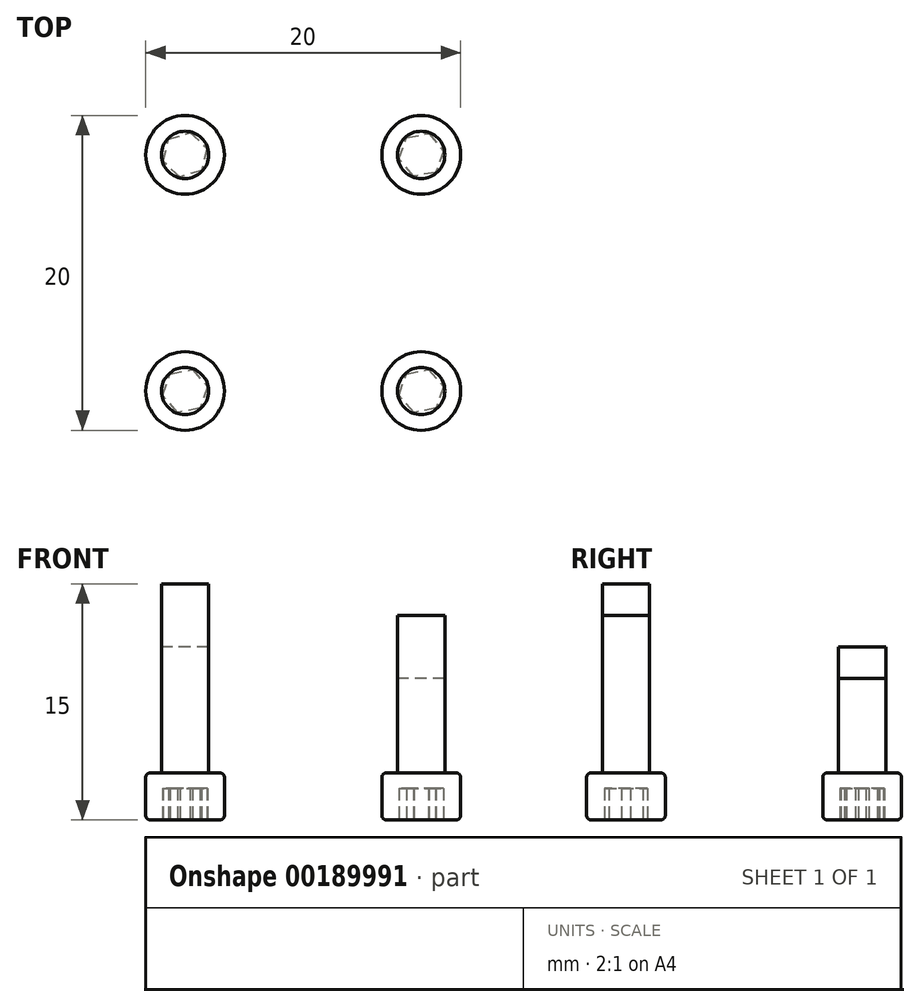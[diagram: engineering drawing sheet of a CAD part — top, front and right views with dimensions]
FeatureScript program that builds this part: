
annotation { "Feature Type Name" : "Feature", "Feature Type Description" : "" }
export const myFeature = defineFeature(function(context is Context, id is Id, definition is map)
    precondition{}
    {
        {
            var Q0;
            Q0=qCreatedBy(makeId("Top.planeOp"),FACE);
            var sketch = newSketch(context, id + "F0", { "sketchPlane" : qUnion([Q0])});
            skLineSegment(sketch, "E0.bottom", {"start": v(7.5, -7.5) * mm, "end": v(-7.5, -7.5) * mm, "construction": true});
            skLineSegment(sketch, "E0.top", {"start": v(7.5, 7.5) * mm, "end": v(-7.5, 7.5) * mm, "construction": true});
            skLineSegment(sketch, "E0.left", {"start": v(7.5, -7.5) * mm, "end": v(7.5, 7.5) * mm, "construction": true});
            skLineSegment(sketch, "E0.right", {"start": v(-7.5, -7.5) * mm, "end": v(-7.5, 7.5) * mm, "construction": true});
            skPoint(sketch, "E0.middle", {"position": v(0, 0) * mm});
            skCircle(sketch, "E1.cCircle", {"center": v(-7.5, 7.5) * mm, "radius": 1.44 * mm, "construction": true});
            skLineSegment(sketch, "E1.0", {"start": v(-6.45, 6.51) * mm, "end": v(-7.83, 6.1) * mm});
            skLineSegment(sketch, "E1.1", {"start": v(-7.83, 6.1) * mm, "end": v(-8.88, 7.08) * mm});
            skLineSegment(sketch, "E1.2", {"start": v(-8.88, 7.08) * mm, "end": v(-8.55, 8.49) * mm});
            skLineSegment(sketch, "E1.3", {"start": v(-8.55, 8.49) * mm, "end": v(-7.17, 8.9) * mm});
            skLineSegment(sketch, "E1.4", {"start": v(-7.17, 8.9) * mm, "end": v(-6.12, 7.92) * mm});
            skLineSegment(sketch, "E1.5", {"start": v(-6.12, 7.92) * mm, "end": v(-6.45, 6.51) * mm});
            skCircle(sketch, "E2.cCircle", {"center": v(7.5, 7.5) * mm, "radius": 1.44 * mm, "construction": true});
            skLineSegment(sketch, "E2.0", {"start": v(8.42, 6.39) * mm, "end": v(7, 6.15) * mm});
            skLineSegment(sketch, "E2.1", {"start": v(7, 6.15) * mm, "end": v(6.08, 7.26) * mm});
            skLineSegment(sketch, "E2.2", {"start": v(6.08, 7.26) * mm, "end": v(6.58, 8.61) * mm});
            skLineSegment(sketch, "E2.3", {"start": v(6.58, 8.61) * mm, "end": v(8, 8.85) * mm});
            skLineSegment(sketch, "E2.4", {"start": v(8, 8.85) * mm, "end": v(8.92, 7.74) * mm});
            skLineSegment(sketch, "E2.5", {"start": v(8.92, 7.74) * mm, "end": v(8.42, 6.39) * mm});
            skCircle(sketch, "E3.cCircle", {"center": v(-7.5, -7.5) * mm, "radius": 1.44 * mm, "construction": true});
            skLineSegment(sketch, "E3.0", {"start": v(-6.55, -8.6) * mm, "end": v(-7.97, -8.86) * mm});
            skLineSegment(sketch, "E3.1", {"start": v(-7.97, -8.86) * mm, "end": v(-8.92, -7.77) * mm});
            skLineSegment(sketch, "E3.2", {"start": v(-8.92, -7.77) * mm, "end": v(-8.45, -6.4) * mm});
            skLineSegment(sketch, "E3.3", {"start": v(-8.45, -6.4) * mm, "end": v(-7.03, -6.14) * mm});
            skLineSegment(sketch, "E3.4", {"start": v(-7.03, -6.14) * mm, "end": v(-6.08, -7.23) * mm});
            skLineSegment(sketch, "E3.5", {"start": v(-6.08, -7.23) * mm, "end": v(-6.55, -8.6) * mm});
            skCircle(sketch, "E4.cCircle", {"center": v(7.5, -7.5) * mm, "radius": 1.44 * mm, "construction": true});
            skLineSegment(sketch, "E4.0", {"start": v(8.45, -8.6) * mm, "end": v(7.03, -8.86) * mm});
            skLineSegment(sketch, "E4.1", {"start": v(7.03, -8.86) * mm, "end": v(6.08, -7.77) * mm});
            skLineSegment(sketch, "E4.2", {"start": v(6.08, -7.77) * mm, "end": v(6.55, -6.4) * mm});
            skLineSegment(sketch, "E4.3", {"start": v(6.55, -6.4) * mm, "end": v(7.97, -6.14) * mm});
            skLineSegment(sketch, "E4.4", {"start": v(7.97, -6.14) * mm, "end": v(8.92, -7.23) * mm});
            skLineSegment(sketch, "E4.5", {"start": v(8.92, -7.23) * mm, "end": v(8.45, -8.6) * mm});
            skCircle(sketch, "E5", {"center": v(-7.5, -7.5) * mm, "radius": 2.5 * mm});
            skCircle(sketch, "E6", {"center": v(7.5, -7.5) * mm, "radius": 2.5 * mm});
            skCircle(sketch, "E7", {"center": v(-7.5, 7.5) * mm, "radius": 2.5 * mm});
            skCircle(sketch, "E8", {"center": v(7.5, 7.5) * mm, "radius": 2.5 * mm});
            skSolve(sketch);
        }
        {
            var Q0;
            Q0 = qSketchRegion(id + "F0", true);
            extrude(context, id + "F1", {"entities" : qUnion([Q0]), "depth" : 2 * mm});
        }
        {
            var Q0;
            Q0=qCreatedBy(makeId("Top.planeOp"),FACE);
            cPlane(context, id + "F2", {"entities" : qUnion([Q0]), "cplaneType" : CPlaneType.OFFSET, "offset" : 2 * mm, "width" : 150 * mm, "height" : 150 * mm});
        }
        {
            var Q0;
            Q0=qCreatedBy(id+"F2.planeOp",FACE);
            var sketch = newSketch(context, id + "F3", { "sketchPlane" : qUnion([Q0])});
            skCircle(sketch, "E9.0", {"center": v(-7.5, 7.5) * mm, "radius": 2.5 * mm});
            skCircle(sketch, "E10.0", {"center": v(-7.5, -7.5) * mm, "radius": 2.5 * mm});
            skCircle(sketch, "E11.0", {"center": v(7.5, -7.5) * mm, "radius": 2.5 * mm});
            skCircle(sketch, "E12.0", {"center": v(7.5, 7.5) * mm, "radius": 2.5 * mm});
            skSolve(sketch);
        }
        {
            var Q0;
            Q0 = qSketchRegion(id + "F3", true);
            extrude(context, id + "F4", {"entities" : qUnion([Q0]), "operationType" : NewBodyOperationType.ADD, "depth" : 1 * mm});
        }
        {
            var Q0;
            Q0=qCreatedBy(id+"F2.planeOp",FACE);
            cPlane(context, id + "F5", {"entities" : qUnion([Q0]), "cplaneType" : CPlaneType.OFFSET, "offset" : 1 * mm, "width" : 150 * mm, "height" : 150 * mm});
        }
        {
            var Q0;
            Q0=qCreatedBy(id+"F5.planeOp",FACE);
            var sketch = newSketch(context, id + "F6", { "sketchPlane" : qUnion([Q0])});
            skPoint(sketch, "E13.0", {"position": v(7.5, 7.5) * mm});
            skCircle(sketch, "E14", {"center": v(7.5, 7.5) * mm, "radius": 1.5 * mm});
            skPoint(sketch, "E15.0", {"position": v(7.5, -7.5) * mm});
            skCircle(sketch, "E16", {"center": v(7.5, -7.5) * mm, "radius": 1.5 * mm});
            skPoint(sketch, "E17.0", {"position": v(-7.5, -7.5) * mm});
            skCircle(sketch, "E18", {"center": v(-7.5, -7.5) * mm, "radius": 1.5 * mm});
            skPoint(sketch, "E19.0", {"position": v(-7.5, 7.5) * mm});
            skCircle(sketch, "E20", {"center": v(-7.5, 7.5) * mm, "radius": 1.5 * mm});
            skSolve(sketch);
        }
        {
            var Q0;
            Q0=makeQuery(id+"F6.imprint","IMPRINT",FACE,{"disambiguationData":[TD([[makeQuery(id+"F6.imprint","IMPRINT",EDGE,{"derivedFrom":sQuery(id+"F6.wireOp",EDGE,"E14")}),1.0]])]});
            extrude(context, id + "F7", {"entities" : qUnion([Q0]), "operationType" : NewBodyOperationType.ADD, "depth" : 6 * mm});
        }
        {
            var Q0;
            Q0=makeQuery(id+"F6.imprint","IMPRINT",FACE,{"disambiguationData":[TD([[makeQuery(id+"F6.imprint","IMPRINT",EDGE,{"derivedFrom":sQuery(id+"F6.wireOp",EDGE,"E20")}),1.0]])]});
            extrude(context, id + "F8", {"entities" : qUnion([Q0]), "operationType" : NewBodyOperationType.ADD, "depth" : 8 * mm});
        }
        {
            var Q0;
            Q0=makeQuery(id+"F6.imprint","IMPRINT",FACE,{"disambiguationData":[TD([[makeQuery(id+"F6.imprint","IMPRINT",EDGE,{"derivedFrom":sQuery(id+"F6.wireOp",EDGE,"E16")}),1.0]])]});
            extrude(context, id + "F9", {"entities" : qUnion([Q0]), "operationType" : NewBodyOperationType.ADD, "depth" : 10 * mm});
        }
        {
            var Q0;
            Q0=makeQuery(id+"F6.imprint","IMPRINT",FACE,{"disambiguationData":[TD([[makeQuery(id+"F6.imprint","IMPRINT",EDGE,{"derivedFrom":sQuery(id+"F6.wireOp",EDGE,"E18")}),1.0]])]});
            extrude(context, id + "F10", {"entities" : qUnion([Q0]), "operationType" : NewBodyOperationType.ADD, "depth" : 12 * mm});
        }
        {
            var Q0;
            Q0=makeQuery(id+"F4.opExtrude","CAP_EDGE",EDGE,{"disambiguationData":[OSD([sQuery(id+"F3.wireOp",EDGE,"E10.0")])],"isStart":false});
            var Q1;
            Q1=makeQuery(id+"F1.opExtrude","CAP_EDGE",EDGE,{"disambiguationData":[OSD([sQuery(id+"F0.wireOp",EDGE,"E5")])],"isStart":true});
            var Q2;
            Q2=makeQuery(id+"F4.opExtrude","CAP_EDGE",EDGE,{"disambiguationData":[OSD([sQuery(id+"F3.wireOp",EDGE,"E9.0")])],"isStart":false});
            var Q3;
            Q3=makeQuery(id+"F1.opExtrude","CAP_EDGE",EDGE,{"disambiguationData":[OSD([sQuery(id+"F0.wireOp",EDGE,"E7")])],"isStart":true});
            var Q4;
            Q4=makeQuery(id+"F4.opExtrude","CAP_EDGE",EDGE,{"disambiguationData":[OSD([sQuery(id+"F3.wireOp",EDGE,"E12.0")])],"isStart":false});
            var Q5;
            Q5=makeQuery(id+"F1.opExtrude","CAP_EDGE",EDGE,{"disambiguationData":[OSD([sQuery(id+"F0.wireOp",EDGE,"E8")])],"isStart":true});
            var Q6;
            Q6=makeQuery(id+"F4.opExtrude","CAP_EDGE",EDGE,{"disambiguationData":[OSD([sQuery(id+"F3.wireOp",EDGE,"E11.0")])],"isStart":false});
            var Q7;
            Q7=makeQuery(id+"F1.opExtrude","CAP_EDGE",EDGE,{"disambiguationData":[OSD([sQuery(id+"F0.wireOp",EDGE,"E6")])],"isStart":true});
            fillet(context, id + "F11", {"entities" : qUnion([Q0, Q1, Q2, Q3, Q4, Q5, Q6, Q7]), "radius" : 0.3 * mm, "tangentPropagation" : true, "allowEdgeOverflow" : false});
        }
    });
